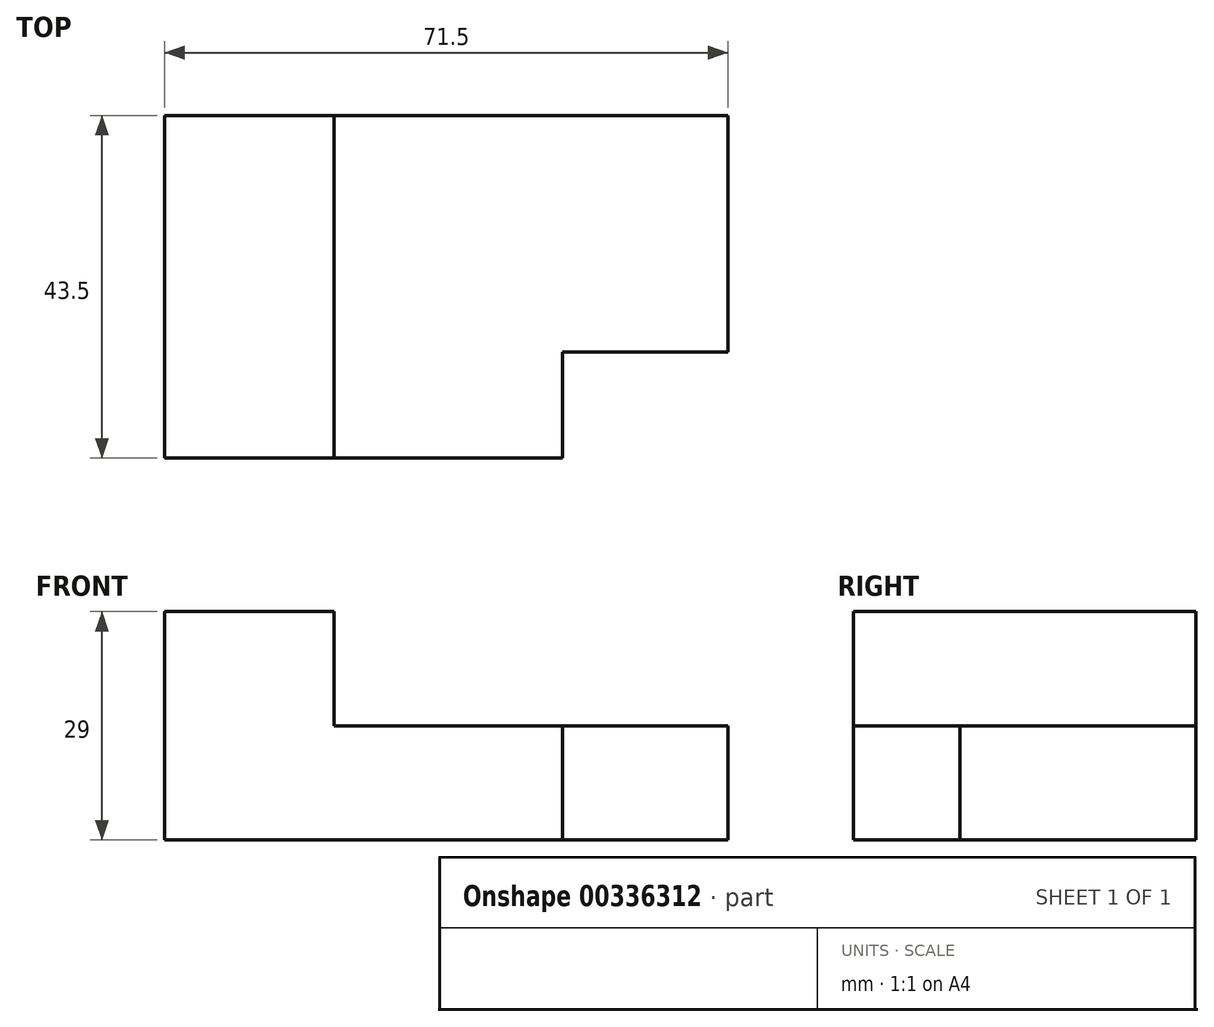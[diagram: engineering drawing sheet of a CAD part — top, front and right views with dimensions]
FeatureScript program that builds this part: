
annotation { "Feature Type Name" : "Feature", "Feature Type Description" : "" }
export const myFeature = defineFeature(function(context is Context, id is Id, definition is map)
    precondition{}
    {
        {
            var Q0;
            Q0=qCreatedBy(makeId("Top.planeOp"),FACE);
            var sketch = newSketch(context, id + "F0", { "sketchPlane" : qUnion([Q0])});
            skLineSegment(sketch, "E0.bottom", {"start": v(0, 0) * mm, "end": v(71.5, 0) * mm});
            skLineSegment(sketch, "E0.top", {"start": v(0, 43.5) * mm, "end": v(71.5, 43.5) * mm});
            skLineSegment(sketch, "E0.left", {"start": v(0, 0) * mm, "end": v(0, 43.5) * mm});
            skLineSegment(sketch, "E0.right", {"start": v(71.5, 0) * mm, "end": v(71.5, 43.5) * mm});
            skSolve(sketch);
        }
        {
            var Q0;
            Q0 = qSketchRegion(id + "F0", true);
            extrude(context, id + "F1", {"entities" : qUnion([Q0]), "depth" : 29 * mm});
        }
        {
            var Q0;
            Q0=makeQuery(id+"F1.opExtrude","CAP_FACE",FACE,{"disambiguationData":[OSD([sQuery(id+"F0.wireOp",EDGE,"E0.bottom"),sQuery(id+"F0.wireOp",EDGE,"E0.top"),sQuery(id+"F0.wireOp",EDGE,"E0.left"),sQuery(id+"F0.wireOp",EDGE,"E0.right")])],"isStart":false});
            var sketch = newSketch(context, id + "F2", { "sketchPlane" : qUnion([Q0])});
            skLineSegment(sketch, "E1.bottom", {"start": v(71.5, 43.5) * mm, "end": v(21.5, 43.5) * mm});
            skLineSegment(sketch, "E1.top", {"start": v(71.5, 0) * mm, "end": v(21.5, 0) * mm});
            skLineSegment(sketch, "E1.left", {"start": v(71.5, 43.5) * mm, "end": v(71.5, 0) * mm});
            skLineSegment(sketch, "E1.right", {"start": v(21.5, 43.5) * mm, "end": v(21.5, 0) * mm});
            skSolve(sketch);
        }
        {
            var Q0;
            Q0 = qSketchRegion(id + "F2", true);
            extrude(context, id + "F3", {"entities" : qUnion([Q0]), "operationType" : NewBodyOperationType.REMOVE, "oppositeDirection" : true, "depth" : 14.5 * mm});
        }
        {
            var Q0;
            Q0=makeQuery(id+"F3.boolean.opBoolean","COPY",FACE,{"derivedFrom":makeQuery(id+"F3.opExtrude","CAP_FACE",FACE,{"disambiguationData":[OSD([sQuery(id+"F2.wireOp",EDGE,"E1.bottom"),sQuery(id+"F2.wireOp",EDGE,"E1.top"),sQuery(id+"F2.wireOp",EDGE,"E1.left"),sQuery(id+"F2.wireOp",EDGE,"E1.right")])],"isStart":false})});
            var sketch = newSketch(context, id + "F4", { "sketchPlane" : qUnion([Q0])});
            skLineSegment(sketch, "E2.bottom", {"start": v(71.5, 0) * mm, "end": v(50.5, 0) * mm});
            skLineSegment(sketch, "E2.top", {"start": v(71.5, 13.5) * mm, "end": v(50.5, 13.5) * mm});
            skLineSegment(sketch, "E2.left", {"start": v(71.5, 0) * mm, "end": v(71.5, 13.5) * mm});
            skLineSegment(sketch, "E2.right", {"start": v(50.5, 0) * mm, "end": v(50.5, 13.5) * mm});
            skSolve(sketch);
        }
        {
            var Q0;
            Q0 = qSketchRegion(id + "F4", true);
            extrude(context, id + "F5", {"entities" : qUnion([Q0]), "operationType" : NewBodyOperationType.REMOVE, "endBound" : BoundingType.THROUGH_ALL, "oppositeDirection" : true, "depth" : 25 * mm});
        }
    });
